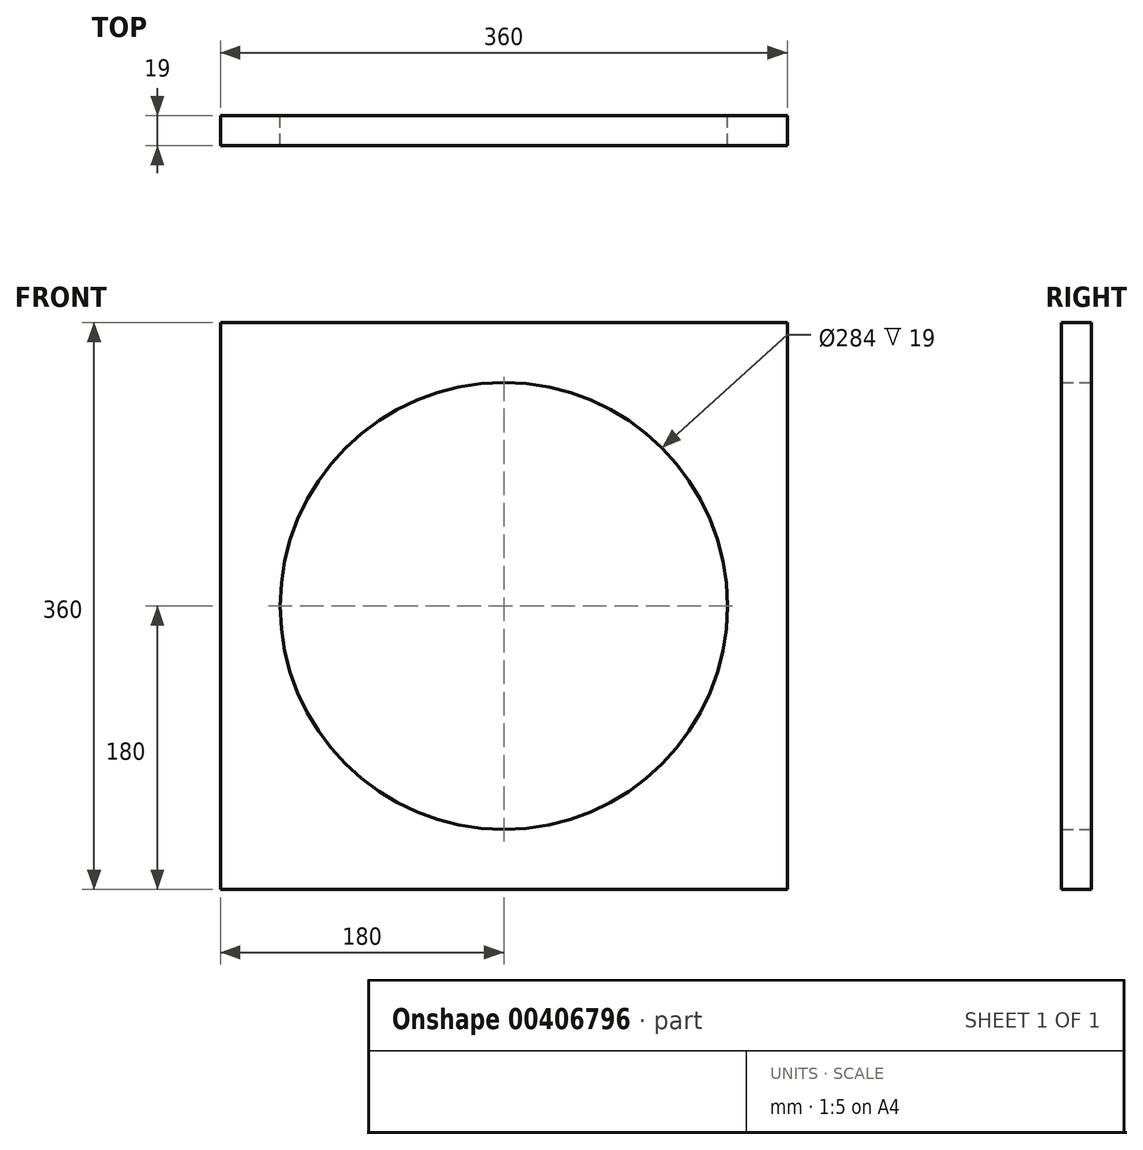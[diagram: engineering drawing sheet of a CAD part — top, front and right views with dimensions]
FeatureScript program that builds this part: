
annotation { "Feature Type Name" : "Feature", "Feature Type Description" : "" }
export const myFeature = defineFeature(function(context is Context, id is Id, definition is map)
    precondition{}
    {
        {
            var Q0;
            Q0=qCreatedBy(makeId("Front.planeOp"),FACE);
            var sketch = newSketch(context, id + "F0", { "sketchPlane" : qUnion([Q0])});
            skLineSegment(sketch, "E0.bottom", {"start": v(0, 0) * mm, "end": v(360, 0) * mm});
            skLineSegment(sketch, "E0.top", {"start": v(0, 360) * mm, "end": v(360, 360) * mm});
            skLineSegment(sketch, "E0.left", {"start": v(0, 0) * mm, "end": v(0, 360) * mm});
            skLineSegment(sketch, "E0.right", {"start": v(360, 0) * mm, "end": v(360, 360) * mm});
            skCircle(sketch, "E1", {"center": v(180, 180) * mm, "radius": 142 * mm});
            skSolve(sketch);
        }
        {
            var Q0;
            Q0=makeQuery(id+"F0.imprint","IMPRINT",FACE,{"disambiguationData":[TD([[makeQuery(id+"F0.imprint","IMPRINT",EDGE,{"derivedFrom":sQuery(id+"F0.wireOp",EDGE,"E0.bottom")}),1.0]])]});
            extrude(context, id + "F1", {"entities" : qUnion([Q0]), "depth" : 19 * mm, "offsetDistance" : 25 * mm});
        }
    });
